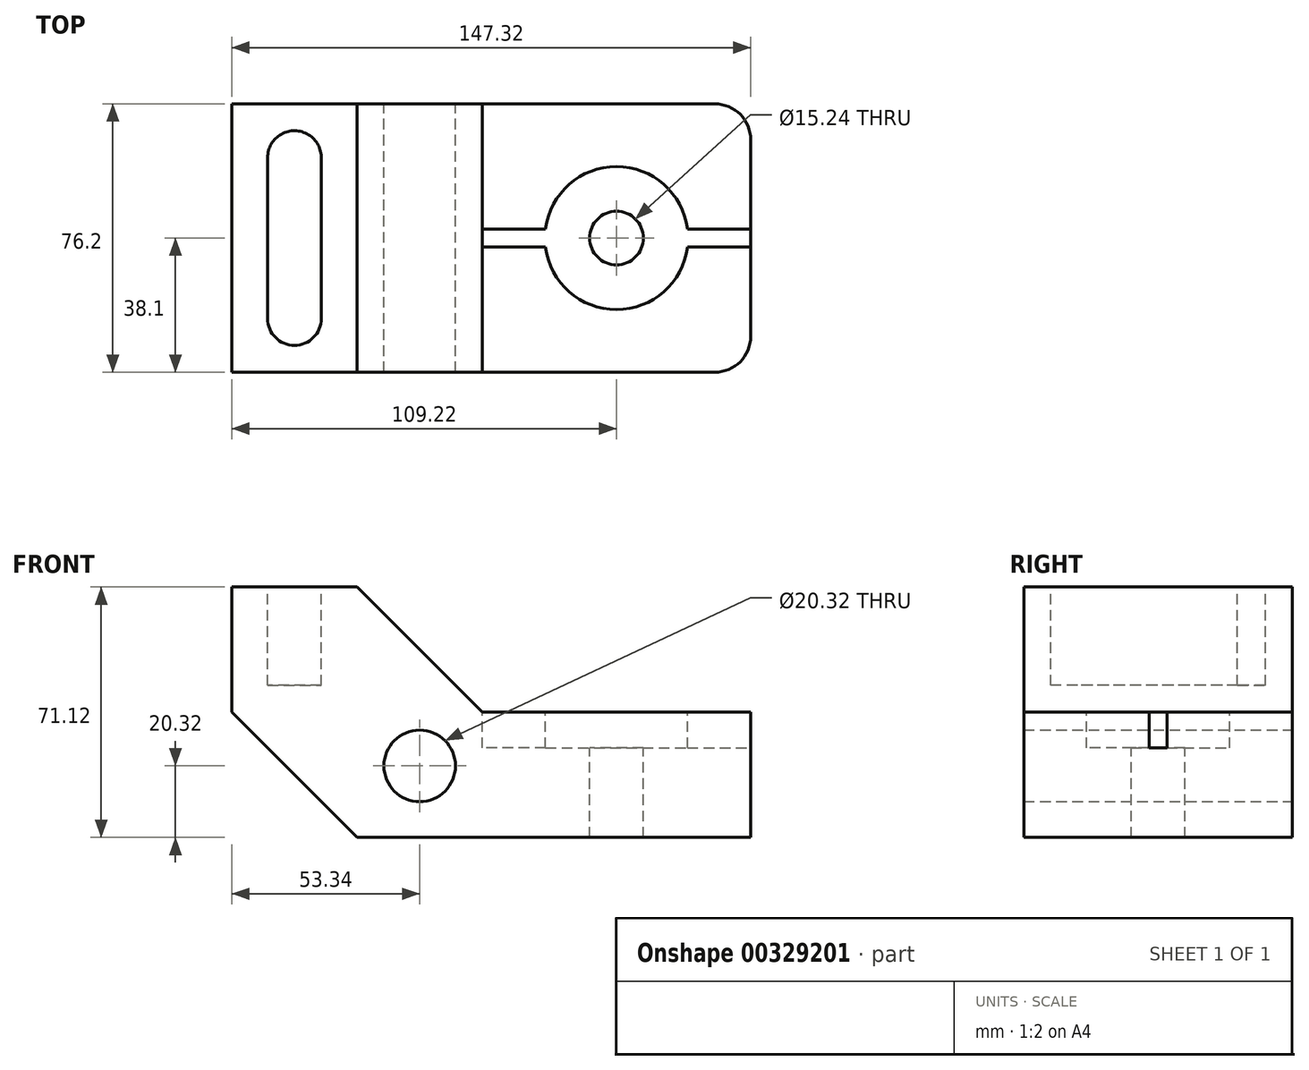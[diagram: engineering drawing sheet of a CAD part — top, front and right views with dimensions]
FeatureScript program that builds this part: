
annotation { "Feature Type Name" : "Feature", "Feature Type Description" : "" }
export const myFeature = defineFeature(function(context is Context, id is Id, definition is map)
    precondition{}
    {
        {
            var Q0;
            Q0=qCreatedBy(makeId("Front.planeOp"),FACE);
            var sketch = newSketch(context, id + "F0", { "sketchPlane" : qUnion([Q0])});
            skLineSegment(sketch, "E0", {"start": v(0, 0) * mm, "end": v(-35.56, 35.56) * mm});
            skLineSegment(sketch, "E1", {"start": v(-35.56, 35.56) * mm, "end": v(-35.56, 71.12) * mm});
            skLineSegment(sketch, "E2", {"start": v(-35.56, 71.12) * mm, "end": v(0, 71.12) * mm});
            skLineSegment(sketch, "E3", {"start": v(0, 71.12) * mm, "end": v(35.56, 35.56) * mm});
            skLineSegment(sketch, "E4", {"start": v(35.56, 35.56) * mm, "end": v(111.76, 35.56) * mm});
            skLineSegment(sketch, "E5", {"start": v(111.76, 35.56) * mm, "end": v(111.76, 0) * mm});
            skLineSegment(sketch, "E6", {"start": v(111.76, 0) * mm, "end": v(0, 0) * mm});
            skSolve(sketch);
        }
        {
            var Q0;
            Q0 = qSketchRegion(id + "F0", true);
            extrude(context, id + "F1", {"entities" : qUnion([Q0]), "depth" : 76.2 * mm});
        }
        {
            var Q0;
            Q0=makeQuery(id+"F1.opExtrude","CAP_EDGE",EDGE,{"disambiguationData":[OSD([sQuery(id+"F0.wireOp",EDGE,"E5")])],"isStart":false});
            var Q1;
            Q1=makeQuery(id+"F1.opExtrude","CAP_EDGE",EDGE,{"disambiguationData":[OSD([sQuery(id+"F0.wireOp",EDGE,"E5")])],"isStart":true});
            fillet(context, id + "F2", {"entities" : qUnion([Q0, Q1]), "radius" : 10.16 * mm, "tangentPropagation" : true, "allowEdgeOverflow" : false});
        }
        {
            var Q0;
            Q0=qCreatedBy(makeId("Front.planeOp"),FACE);
            var sketch = newSketch(context, id + "F3", { "sketchPlane" : qUnion([Q0])});
            skCircle(sketch, "E7", {"center": v(17.78, 20.32) * mm, "radius": 10.16 * mm});
            skSolve(sketch);
        }
        {
            var Q0;
            Q0 = qSketchRegion(id + "F3", true);
            extrude(context, id + "F4", {"entities" : qUnion([Q0]), "operationType" : NewBodyOperationType.REMOVE, "endBound" : BoundingType.THROUGH_ALL, "depth" : 25.4 * mm});
        }
        {
            var Q0;
            Q0=makeQuery(id+"F1.opExtrude","SWEPT_FACE",FACE,{"disambiguationData":[OSD([sQuery(id+"F0.wireOp",EDGE,"E2")])]});
            var sketch = newSketch(context, id + "F5", { "sketchPlane" : qUnion([Q0])});
            skLineSegment(sketch, "E8", {"start": v(-25.4, -15.24) * mm, "end": v(-25.4, -60.96) * mm});
            skLineSegment(sketch, "E9", {"start": v(-10.17, -15.53) * mm, "end": v(-10.17, -60.96) * mm});
            skArc(sketch, "E10", {"start": v(-10.17, -15.53) * mm, "mid": v(-17.64, -7.62) * mm, "end": v(-25.4, -15.24) * mm});
            skArc(sketch, "E11", {"start": v(-25.4, -60.96) * mm, "mid": v(-17.78, -68.58) * mm, "end": v(-10.17, -60.96) * mm});
            skSolve(sketch);
        }
        {
            var Q0;
            Q0 = qSketchRegion(id + "F5", true);
            extrude(context, id + "F6", {"entities" : qUnion([Q0]), "operationType" : NewBodyOperationType.REMOVE, "oppositeDirection" : true, "depth" : 27.94 * mm});
        }
        {
            var Q0;
            Q0=makeQuery(id+"F1.opExtrude","SWEPT_FACE",FACE,{"disambiguationData":[OSD([sQuery(id+"F0.wireOp",EDGE,"E4")])]});
            var sketch = newSketch(context, id + "F7", { "sketchPlane" : qUnion([Q0])});
            skCircle(sketch, "E12", {"center": v(73.66, -38.1) * mm, "radius": 20.32 * mm});
            skLineSegment(sketch, "E13", {"start": v(93.82, -35.56) * mm, "end": v(111.76, -35.56) * mm});
            skLineSegment(sketch, "E14", {"start": v(93.82, -40.64) * mm, "end": v(111.76, -40.64) * mm});
            skLineSegment(sketch, "E15", {"start": v(53.5, -35.56) * mm, "end": v(35.56, -35.56) * mm});
            skLineSegment(sketch, "E16", {"start": v(53.5, -40.64) * mm, "end": v(35.56, -40.64) * mm});
            skLineSegment(sketch, "E17", {"start": v(111.76, -35.56) * mm, "end": v(111.76, -40.64) * mm});
            skLineSegment(sketch, "E18", {"start": v(35.56, -35.56) * mm, "end": v(35.56, -40.64) * mm});
            skSolve(sketch);
        }
        {
            var Q0;
            Q0 = qSketchRegion(id + "F7", true);
            extrude(context, id + "F8", {"entities" : qUnion([Q0]), "operationType" : NewBodyOperationType.REMOVE, "oppositeDirection" : true, "depth" : 10.16 * mm});
        }
        {
            var Q0;
            Q0=makeQuery(id+"F8.boolean.opBoolean","COPY",FACE,{"derivedFrom":makeQuery(id+"F8.opExtrude","CAP_FACE",FACE,{"disambiguationData":[OSD([sQuery(id+"F7.wireOp",EDGE,"E12"),sQuery(id+"F7.wireOp",EDGE,"E13"),sQuery(id+"F7.wireOp",EDGE,"E14"),sQuery(id+"F7.wireOp",EDGE,"E15"),sQuery(id+"F7.wireOp",EDGE,"E16"),sQuery(id+"F7.wireOp",EDGE,"E17"),sQuery(id+"F7.wireOp",EDGE,"E18")])],"isStart":false})});
            var sketch = newSketch(context, id + "F9", { "sketchPlane" : qUnion([Q0])});
            skCircle(sketch, "E19", {"center": v(73.66, -38.1) * mm, "radius": 7.62 * mm});
            skSolve(sketch);
        }
        {
            var Q0;
            Q0 = qSketchRegion(id + "F9", true);
            extrude(context, id + "F10", {"entities" : qUnion([Q0]), "operationType" : NewBodyOperationType.REMOVE, "endBound" : BoundingType.THROUGH_ALL, "oppositeDirection" : true, "depth" : 25.4 * mm});
        }
    });
